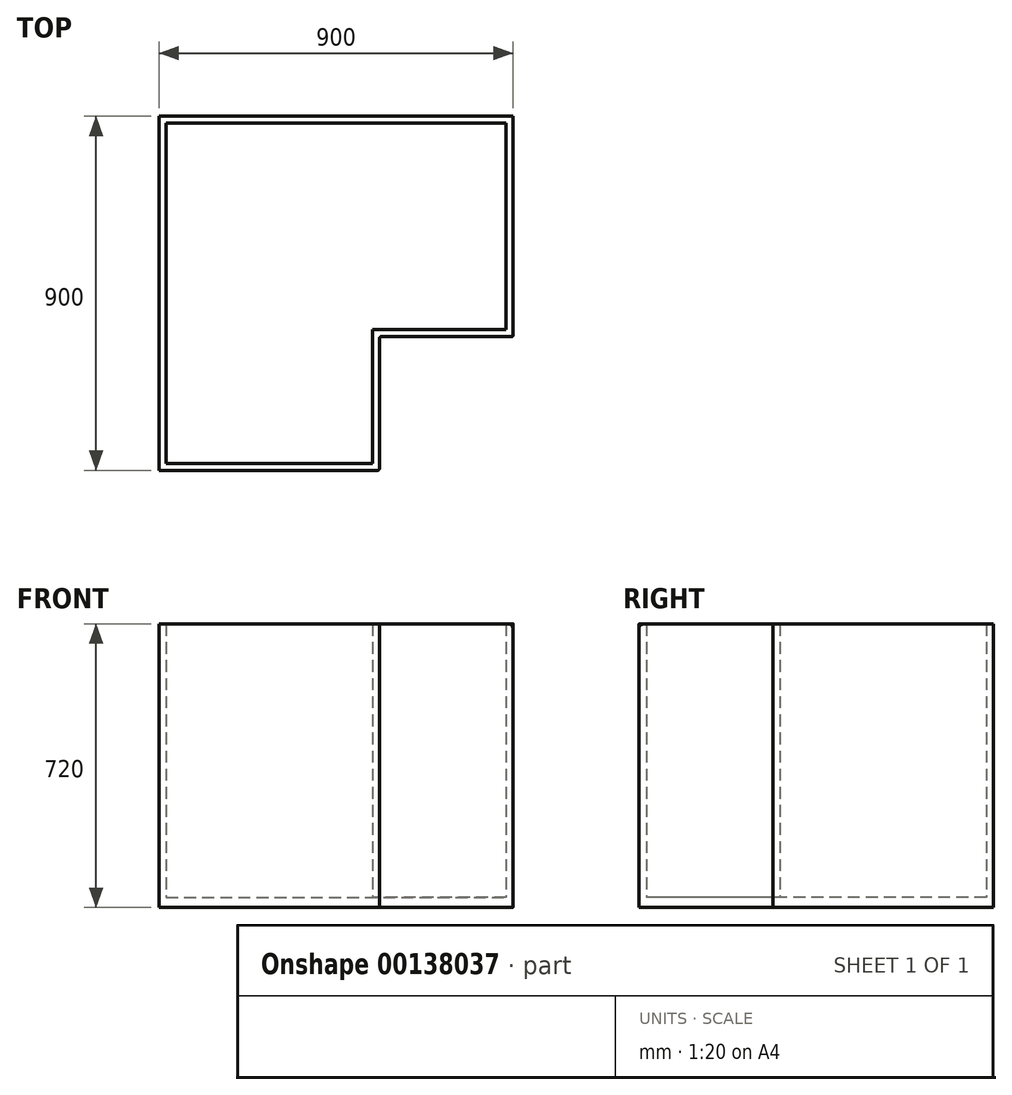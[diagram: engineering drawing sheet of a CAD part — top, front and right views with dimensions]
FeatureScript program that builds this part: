
annotation { "Feature Type Name" : "Feature", "Feature Type Description" : "" }
export const myFeature = defineFeature(function(context is Context, id is Id, definition is map)
    precondition{}
    {
        {
            var Q0;
            Q0=qCreatedBy(makeId("Top.planeOp"),FACE);
            var sketch = newSketch(context, id + "F0", { "sketchPlane" : qUnion([Q0])});
            skLineSegment(sketch, "E0.bottom", {"start": v(-448.91, 564.32) * mm, "end": v(451.09, 564.32) * mm});
            skLineSegment(sketch, "E0.top", {"start": v(-448.91, -335.68) * mm, "end": v(111.09, -335.68) * mm});
            skLineSegment(sketch, "E0.left", {"start": v(-448.91, 564.32) * mm, "end": v(-448.91, -335.68) * mm});
            skLineSegment(sketch, "E0.right", {"start": v(451.09, 564.32) * mm, "end": v(451.09, 4.32) * mm});
            skLineSegment(sketch, "E1", {"start": v(451.09, 4.32) * mm, "end": v(111.09, 4.32) * mm});
            skLineSegment(sketch, "E2", {"start": v(111.09, 4.32) * mm, "end": v(111.09, -335.68) * mm});
            skLineSegment(sketch, "E3.0", {"start": v(-430.91, 546.32) * mm, "end": v(-430.91, -317.68) * mm});
            skLineSegment(sketch, "E3.1", {"start": v(433.09, 546.32) * mm, "end": v(433.09, 22.32) * mm});
            skLineSegment(sketch, "E3.2", {"start": v(433.09, 22.32) * mm, "end": v(93.09, 22.32) * mm});
            skLineSegment(sketch, "E3.3", {"start": v(-430.91, 546.32) * mm, "end": v(433.09, 546.32) * mm});
            skLineSegment(sketch, "E3.4", {"start": v(93.09, 22.32) * mm, "end": v(93.09, -317.68) * mm});
            skLineSegment(sketch, "E3.5", {"start": v(-430.91, -317.68) * mm, "end": v(93.09, -317.68) * mm});
            skSolve(sketch);
        }
        {
            var Q0;
            Q0=makeQuery(id+"F0.imprint","IMPRINT",FACE,{"disambiguationData":[TD([[makeQuery(id+"F0.imprint","IMPRINT",EDGE,{"derivedFrom":sQuery(id+"F0.wireOp",EDGE,"E0.bottom")}),-1.0]])]});
            extrude(context, id + "F1", {"entities" : qUnion([Q0]), "depth" : 720 * mm});
        }
        {
            var Q0;
            Q0=makeQuery(id+"F0.imprint","IMPRINT",FACE,{"disambiguationData":[TD([[makeQuery(id+"F0.imprint","IMPRINT",EDGE,{"derivedFrom":sQuery(id+"F0.wireOp",EDGE,"E3.0")}),1.0]])]});
            extrude(context, id + "F2", {"entities" : qUnion([Q0]), "operationType" : NewBodyOperationType.ADD, "depth" : 25 * mm});
        }
        {
            var Q0;
            Q0=makeQuery(id+"F1.opExtrude","SWEPT_EDGE",EDGE,{"disambiguationData":[OSD([sQuery(id+"F0.wireOp",EDGE,"E0.right"),sQuery(id+"F0.wireOp",EDGE,"E1")])]});
            var Q1;
            Q1=makeQuery(id+"F1.opExtrude","SWEPT_EDGE",EDGE,{"disambiguationData":[OSD([sQuery(id+"F0.wireOp",EDGE,"E1"),sQuery(id+"F0.wireOp",EDGE,"E2")])]});
            var Q2;
            Q2=makeQuery(id+"F1.opExtrude","SWEPT_EDGE",EDGE,{"disambiguationData":[OSD([sQuery(id+"F0.wireOp",EDGE,"E0.top"),sQuery(id+"F0.wireOp",EDGE,"E2")])]});
            var Q3;
            Q3=makeQuery(id+"F1.opExtrude","CAP_EDGE",EDGE,{"disambiguationData":[OSD([sQuery(id+"F0.wireOp",EDGE,"E1")])],"isStart":false});
            var Q4;
            Q4=makeQuery(id+"F1.opExtrude","CAP_EDGE",EDGE,{"disambiguationData":[OSD([sQuery(id+"F0.wireOp",EDGE,"E2")])],"isStart":false});
            fillet(context, id + "F3", {"entities" : qUnion([Q0, Q1, Q2, Q3, Q4]), "radius" : 5 * mm, "tangentPropagation" : true, "allowEdgeOverflow" : false});
        }
    });
